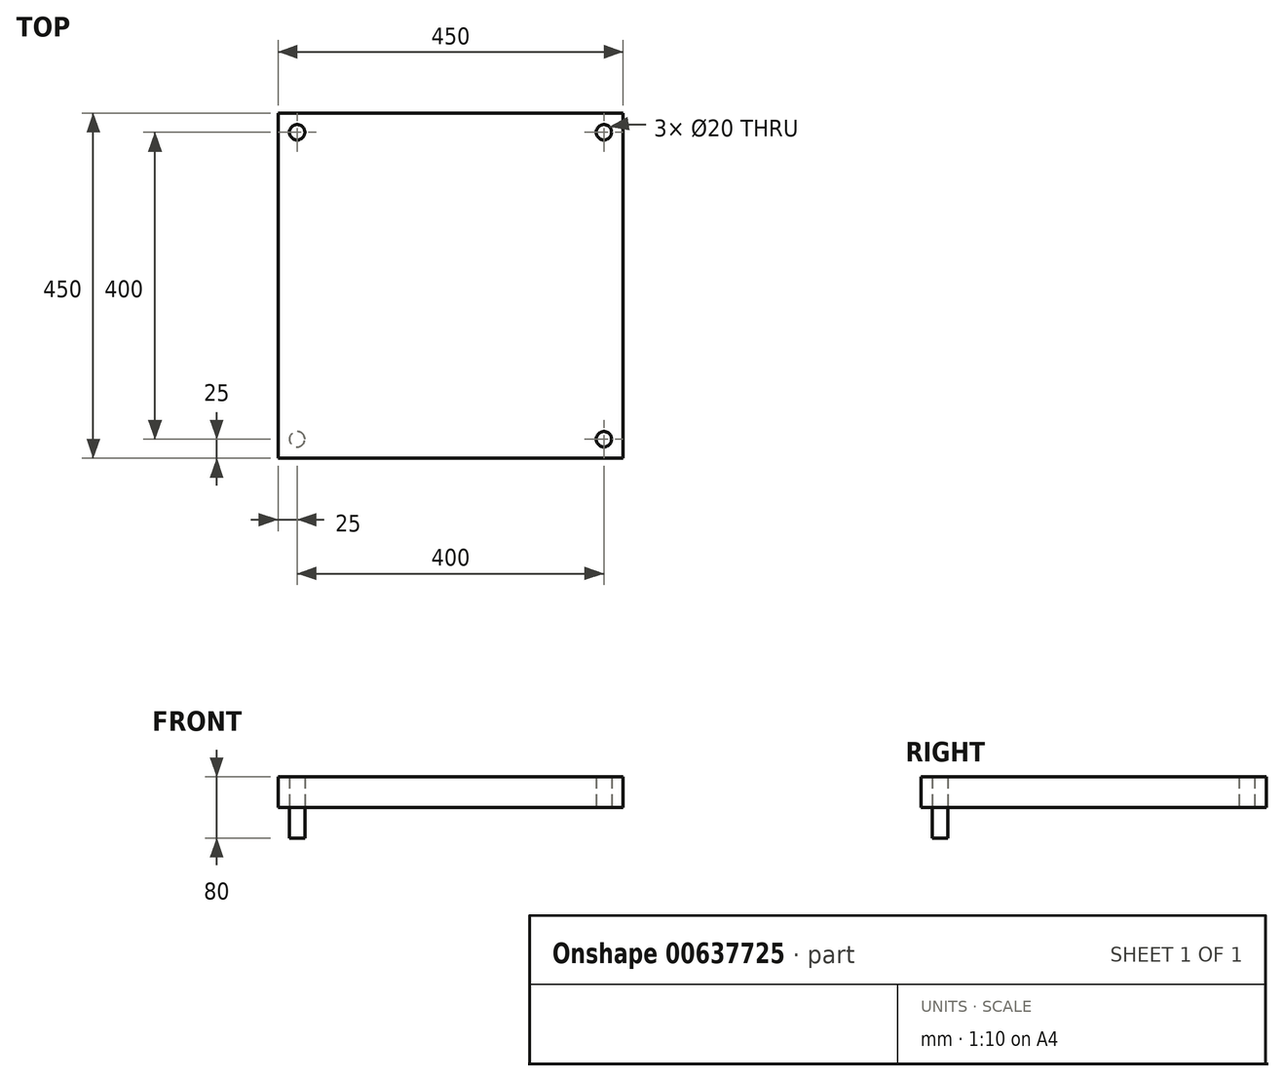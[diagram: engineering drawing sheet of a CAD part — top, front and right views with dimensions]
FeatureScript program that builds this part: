
annotation { "Feature Type Name" : "Feature", "Feature Type Description" : "" }
export const myFeature = defineFeature(function(context is Context, id is Id, definition is map)
    precondition{}
    {
        {
            var Q0;
            Q0=qCreatedBy(makeId("Top.planeOp"),FACE);
            var sketch = newSketch(context, id + "F0", { "sketchPlane" : qUnion([Q0])});
            skLineSegment(sketch, "E0.bottom", {"start": v(225, 225) * mm, "end": v(-225, 225) * mm});
            skLineSegment(sketch, "E0.top", {"start": v(225, -225) * mm, "end": v(-225, -225) * mm});
            skLineSegment(sketch, "E0.left", {"start": v(225, 225) * mm, "end": v(225, -225) * mm});
            skLineSegment(sketch, "E0.right", {"start": v(-225, 225) * mm, "end": v(-225, -225) * mm});
            skPoint(sketch, "E0.middle", {"position": v(0, 0) * mm});
            skCircle(sketch, "E1", {"center": v(-200, 200) * mm, "radius": 10 * mm});
            skCircle(sketch, "E2", {"center": v(200, 200) * mm, "radius": 10 * mm});
            skCircle(sketch, "E3", {"center": v(-200, -200) * mm, "radius": 10 * mm});
            skCircle(sketch, "E4", {"center": v(200, -200) * mm, "radius": 10 * mm});
            skSolve(sketch);
        }
        {
            var Q0;
            Q0=makeQuery(id+"F0.imprint","IMPRINT",FACE,{"disambiguationData":[TD([[makeQuery(id+"F0.imprint","IMPRINT",EDGE,{"derivedFrom":sQuery(id+"F0.wireOp",EDGE,"E0.bottom")}),1.0]])]});
            extrude(context, id + "F1", {"entities" : qUnion([Q0]), "depth" : 40 * mm, "offsetDistance" : 25 * mm});
        }
        {
            var Q0;
            Q0=makeQuery(id+"F1.opExtrude","CAP_FACE",FACE,{"disambiguationData":[OSD([sQuery(id+"F0.wireOp",EDGE,"E0.bottom"),sQuery(id+"F0.wireOp",EDGE,"E0.top"),sQuery(id+"F0.wireOp",EDGE,"E0.left"),sQuery(id+"F0.wireOp",EDGE,"E0.right"),sQuery(id+"F0.wireOp",EDGE,"E1"),sQuery(id+"F0.wireOp",EDGE,"E2"),sQuery(id+"F0.wireOp",EDGE,"E3"),sQuery(id+"F0.wireOp",EDGE,"E4")])],"isStart":false});
            var sketch = newSketch(context, id + "F2", { "sketchPlane" : qUnion([Q0])});
            skCircle(sketch, "E5.0", {"center": v(-200, -200) * mm, "radius": 10 * mm});
            skSolve(sketch);
        }
        {
            var Q0;
            Q0 = qSketchRegion(id + "F2", true);
            extrude(context, id + "F3", {"entities" : qUnion([Q0]), "operationType" : NewBodyOperationType.ADD, "oppositeDirection" : true, "depth" : 80 * mm, "offsetDistance" : 25 * mm});
        }
        {
            var Q0;
            Q0=makeQuery(id+"F1.opExtrude","CAP_FACE",FACE,{"disambiguationData":[OSD([sQuery(id+"F0.wireOp",EDGE,"E0.bottom"),sQuery(id+"F0.wireOp",EDGE,"E0.top"),sQuery(id+"F0.wireOp",EDGE,"E0.left"),sQuery(id+"F0.wireOp",EDGE,"E0.right"),sQuery(id+"F0.wireOp",EDGE,"E1"),sQuery(id+"F0.wireOp",EDGE,"E2"),sQuery(id+"F0.wireOp",EDGE,"E3"),sQuery(id+"F0.wireOp",EDGE,"E4")])],"isStart":true});
            var sketch = newSketch(context, id + "F4", { "sketchPlane" : qUnion([Q0])});
            skCircle(sketch, "E6", {"center": v(-200, 200) * mm, "radius": 25 * mm});
            skSolve(sketch);
        }
        {
            var Q0;
            Q0=sQuery(id+"F4.wireOp",EDGE,"E6");
            extrude(context, id + "F5", {"bodyType" : ToolBodyType.SURFACE, "surfaceEntities" : qUnion([Q0]), "depth" : 420 * mm, "offsetDistance" : 25 * mm});
        }
    });
